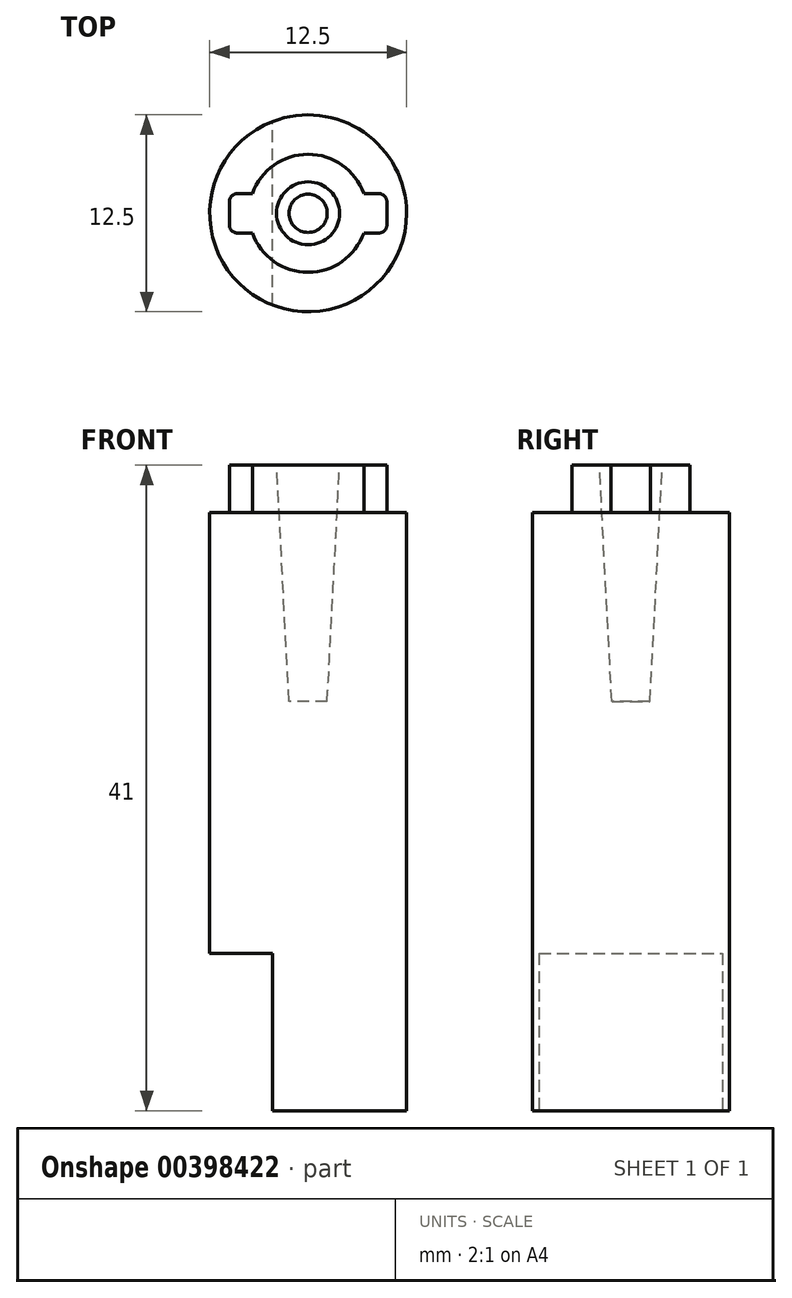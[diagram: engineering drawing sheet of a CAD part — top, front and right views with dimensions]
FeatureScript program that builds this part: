
annotation { "Feature Type Name" : "Feature", "Feature Type Description" : "" }
export const myFeature = defineFeature(function(context is Context, id is Id, definition is map)
    precondition{}
    {
        {
            var Q0;
            Q0=qCreatedBy(makeId("Top.planeOp"),FACE);
            var sketch = newSketch(context, id + "F0", { "sketchPlane" : qUnion([Q0])});
            skCircle(sketch, "E0", {"center": v(0, 0) * mm, "radius": 6.25 * mm});
            skSolve(sketch);
        }
        {
            var Q0;
            Q0 = qSketchRegion(id + "F0", true);
            extrude(context, id + "F1", {"entities" : qUnion([Q0]), "depth" : 38 * mm});
        }
        {
            var Q0;
            Q0=makeQuery(id+"F1.opExtrude","CAP_FACE",FACE,{"disambiguationData":[OSD([sQuery(id+"F0.wireOp",EDGE,"E0")])],"isStart":false});
            var sketch = newSketch(context, id + "F2", { "sketchPlane" : qUnion([Q0])});
            skCircle(sketch, "E1", {"center": v(0, 0) * mm, "radius": 3.75 * mm});
            skLineSegment(sketch, "E2.bottom", {"start": v(4.5, 1.25) * mm, "end": v(-4.5, 1.25) * mm});
            skLineSegment(sketch, "E2.top", {"start": v(4.5, -1.25) * mm, "end": v(-4.5, -1.25) * mm});
            skLineSegment(sketch, "E2.left", {"start": v(5, 0.75) * mm, "end": v(5, -0.75) * mm});
            skLineSegment(sketch, "E2.right", {"start": v(-5, 0.75) * mm, "end": v(-5, -0.75) * mm});
            skPoint(sketch, "E3.visualSharp", {"position": v(-5, 1.25) * mm});
            skArc(sketch, "E3.filletArc", {"start": v(-4.5, 1.25) * mm, "mid": v(-4.85, 1.1) * mm, "end": v(-5, 0.75) * mm});
            skPoint(sketch, "E4.visualSharp", {"position": v(-5, -1.25) * mm});
            skArc(sketch, "E4.filletArc", {"start": v(-5, -0.75) * mm, "mid": v(-4.85, -1.1) * mm, "end": v(-4.5, -1.25) * mm});
            skPoint(sketch, "E5.visualSharp", {"position": v(5, -1.25) * mm});
            skArc(sketch, "E5.filletArc", {"start": v(4.5, -1.25) * mm, "mid": v(4.85, -1.1) * mm, "end": v(5, -0.75) * mm});
            skPoint(sketch, "E6.visualSharp", {"position": v(5, 1.25) * mm});
            skArc(sketch, "E6.filletArc", {"start": v(5, 0.75) * mm, "mid": v(4.85, 1.1) * mm, "end": v(4.5, 1.25) * mm});
            skSolve(sketch);
        }
        {
            var Q0;
            Q0 = qSketchRegion(id + "F2", true);
            extrude(context, id + "F3", {"entities" : qUnion([Q0]), "operationType" : NewBodyOperationType.ADD, "depth" : 3 * mm});
        }
        {
            var Q0;
            Q0=makeQuery(id+"F3.opExtrude","CAP_FACE",FACE,{"disambiguationData":[OSD([sQuery(id+"F2.wireOp",EDGE,"E1"),sQuery(id+"F2.wireOp",EDGE,"E2.bottom"),sQuery(id+"F2.wireOp",EDGE,"E2.top"),sQuery(id+"F2.wireOp",EDGE,"E2.left"),sQuery(id+"F2.wireOp",EDGE,"E2.right"),sQuery(id+"F2.wireOp",EDGE,"E3.filletArc"),sQuery(id+"F2.wireOp",EDGE,"E4.filletArc"),sQuery(id+"F2.wireOp",EDGE,"E5.filletArc"),sQuery(id+"F2.wireOp",EDGE,"E6.filletArc")])],"isStart":false});
            var sketch = newSketch(context, id + "F4", { "sketchPlane" : qUnion([Q0])});
            skCircle(sketch, "E7", {"center": v(0, 0) * mm, "radius": 2 * mm});
            skSolve(sketch);
        }
        {
            var Q0;
            Q0=makeQuery(id+"F4.imprint","IMPRINT",FACE,{"disambiguationData":[TD([[makeQuery(id+"F4.imprint","IMPRINT",EDGE,{"derivedFrom":sQuery(id+"F4.wireOp",EDGE,"E7")}),1.0]])]});
            extrude(context, id + "F5", {"entities" : qUnion([Q0]), "operationType" : NewBodyOperationType.REMOVE, "oppositeDirection" : true, "depth" : 15 * mm, "hasDraft" : true, "draftAngle" : 3 * degree, "draftPullDirection" : true});
        }
        {
            var Q0;
            Q0=makeQuery(id+"F1.opExtrude","CAP_FACE",FACE,{"disambiguationData":[OSD([sQuery(id+"F0.wireOp",EDGE,"E0")])],"isStart":true});
            var sketch = newSketch(context, id + "F6", { "sketchPlane" : qUnion([Q0])});
            skLineSegment(sketch, "E8.bottom", {"start": v(-2.25, 7.5) * mm, "end": v(-10.25, 7.5) * mm});
            skLineSegment(sketch, "E8.top", {"start": v(-2.25, -7.5) * mm, "end": v(-10.25, -7.5) * mm});
            skLineSegment(sketch, "E8.left", {"start": v(-2.25, 7.5) * mm, "end": v(-2.25, -7.5) * mm});
            skLineSegment(sketch, "E8.right", {"start": v(-10.25, 7.5) * mm, "end": v(-10.25, -7.5) * mm});
            skPoint(sketch, "E8.middle", {"position": v(-6.25, 0) * mm});
            skSolve(sketch);
        }
        {
            var Q0;
            Q0 = qSketchRegion(id + "F6", true);
            extrude(context, id + "F7", {"entities" : qUnion([Q0]), "operationType" : NewBodyOperationType.REMOVE, "oppositeDirection" : true, "depth" : 10 * mm});
        }
    });
